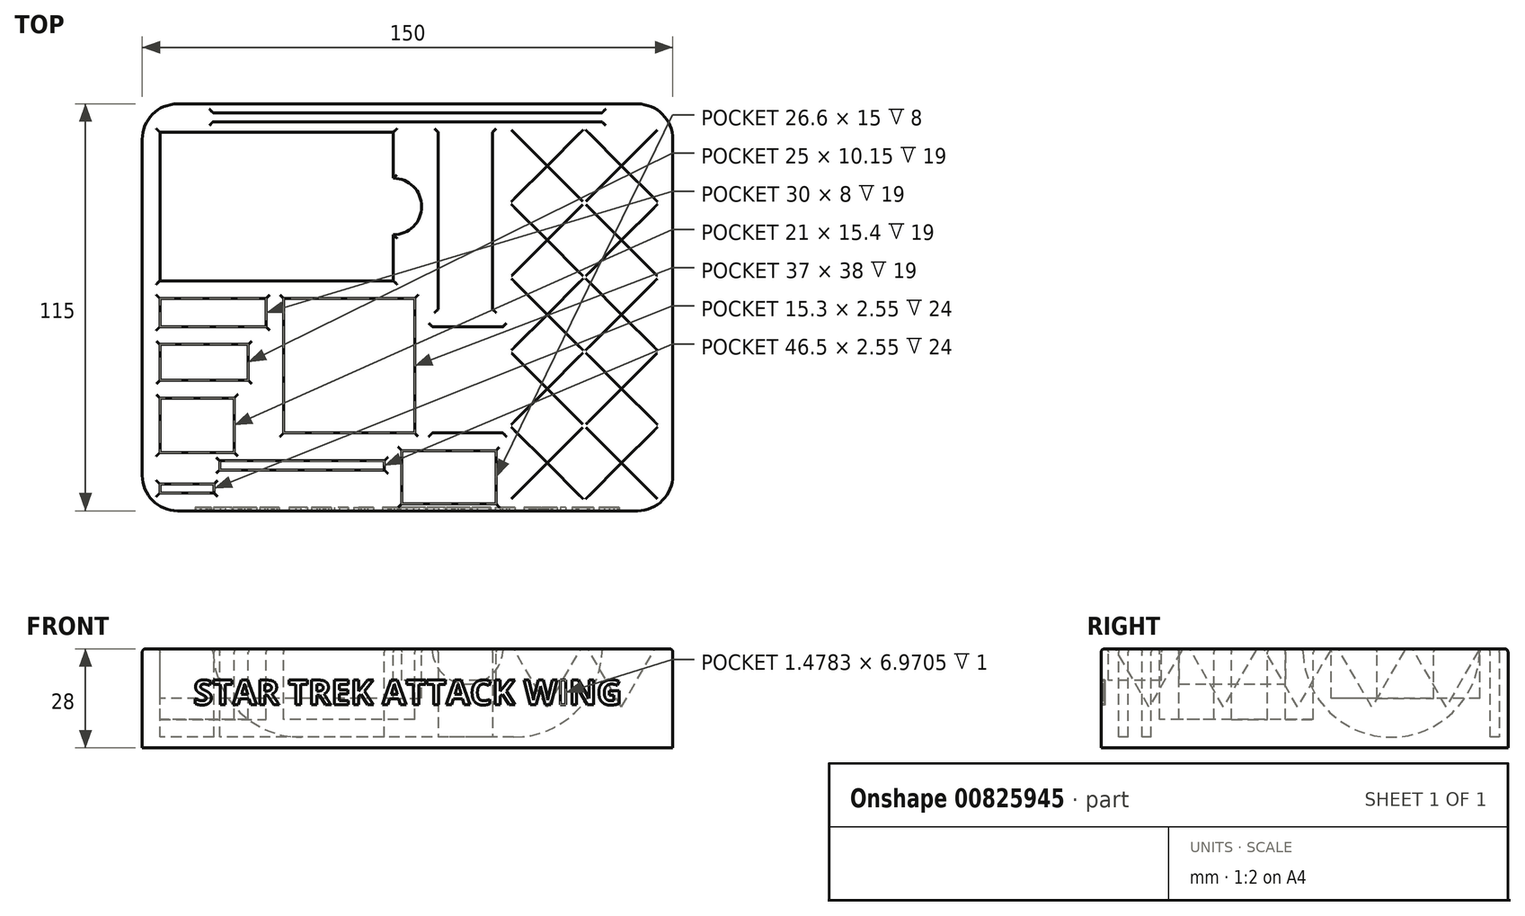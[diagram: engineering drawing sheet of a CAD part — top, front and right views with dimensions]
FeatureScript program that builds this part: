
annotation { "Feature Type Name" : "Feature", "Feature Type Description" : "" }
export const myFeature = defineFeature(function(context is Context, id is Id, definition is map)
    precondition{}
    {
        {
            var Q0;
            Q0=qCreatedBy(makeId("Top.planeOp"),FACE);
            var sketch = newSketch(context, id + "F0", { "sketchPlane" : qUnion([Q0])});
            skLineSegment(sketch, "E0.bottom", {"start": v(75, 57.5) * mm, "end": v(-75, 57.5) * mm});
            skLineSegment(sketch, "E0.top", {"start": v(75, -57.5) * mm, "end": v(-75, -57.5) * mm});
            skLineSegment(sketch, "E0.left", {"start": v(75, 57.5) * mm, "end": v(75, -57.5) * mm});
            skLineSegment(sketch, "E0.right", {"start": v(-75, 57.5) * mm, "end": v(-75, -57.5) * mm});
            skPoint(sketch, "E0.middle", {"position": v(0, 0) * mm});
            skSolve(sketch);
        }
        {
            var Q0;
            Q0 = qSketchRegion(id + "F0", true);
            extrude(context, id + "F1", {"entities" : qUnion([Q0]), "depth" : 28 * mm, "offsetDistance" : 25 * mm});
        }
        {
            var Q0;
            Q0=makeQuery(id+"F1.opExtrude","CAP_FACE",FACE,{"disambiguationData":[OSD([sQuery(id+"F0.wireOp",EDGE,"E0.bottom"),sQuery(id+"F0.wireOp",EDGE,"E0.top"),sQuery(id+"F0.wireOp",EDGE,"E0.left"),sQuery(id+"F0.wireOp",EDGE,"E0.right")])],"isStart":false});
            var sketch = newSketch(context, id + "F2", { "sketchPlane" : qUnion([Q0])});
            skLineSegment(sketch, "E1.bottom", {"start": v(-4, 49.5) * mm, "end": v(-70, 49.5) * mm});
            skLineSegment(sketch, "E1.top", {"start": v(-4, 7.5) * mm, "end": v(-70, 7.5) * mm});
            skLineSegment(sketch, "E1.left", {"start": v(-4, 49.5) * mm, "end": v(-4, 7.5) * mm});
            skLineSegment(sketch, "E1.right", {"start": v(-70, 49.5) * mm, "end": v(-70, 7.5) * mm});
            skPoint(sketch, "E1.middle", {"position": v(-37, 28.5) * mm});
            skArc(sketch, "E2", {"start": v(-4, 20.5) * mm, "mid": v(4, 28.5) * mm, "end": v(-4, 36.5) * mm});
            skSolve(sketch);
        }
        {
            var Q0;
            Q0 = qSketchRegion(id + "F2", true);
            extrude(context, id + "F3", {"entities" : qUnion([Q0]), "operationType" : NewBodyOperationType.REMOVE, "oppositeDirection" : true, "depth" : 14 * mm, "offsetDistance" : 25 * mm});
        }
        {
            var Q0;
            Q0=makeQuery(id+"F1.opExtrude","CAP_FACE",FACE,{"disambiguationData":[OSD([sQuery(id+"F0.wireOp",EDGE,"E0.bottom"),sQuery(id+"F0.wireOp",EDGE,"E0.top"),sQuery(id+"F0.wireOp",EDGE,"E0.left"),sQuery(id+"F0.wireOp",EDGE,"E0.right")])],"isStart":false});
            var sketch = newSketch(context, id + "F4", { "sketchPlane" : qUnion([Q0])});
            skLineSegment(sketch, "E3.bottom", {"start": v(70, 49.5) * mm, "end": v(51, 49.5) * mm});
            skLineSegment(sketch, "E3.top", {"start": v(70, 30.5) * mm, "end": v(51, 30.5) * mm});
            skLineSegment(sketch, "E3.left", {"start": v(70, 49.5) * mm, "end": v(70, 30.5) * mm});
            skLineSegment(sketch, "E3.right", {"start": v(51, 49.5) * mm, "end": v(51, 30.5) * mm});
            skPoint(sketch, "E3.middle", {"position": v(60.5, 40) * mm});
            skLineSegment(sketch, "E4.0.1.0", {"start": v(70, 28.5) * mm, "end": v(51, 28.5) * mm});
            skLineSegment(sketch, "E4.0.1.1", {"start": v(51, 28.5) * mm, "end": v(51, 9.5) * mm});
            skLineSegment(sketch, "E4.0.1.2", {"start": v(70, 28.5) * mm, "end": v(70, 9.5) * mm});
            skLineSegment(sketch, "E4.0.1.3", {"start": v(70, 9.5) * mm, "end": v(51, 9.5) * mm});
            skLineSegment(sketch, "E4.0.2.0", {"start": v(70, 7.5) * mm, "end": v(51, 7.5) * mm});
            skLineSegment(sketch, "E4.0.2.1", {"start": v(51, 7.5) * mm, "end": v(51, -11.5) * mm});
            skLineSegment(sketch, "E4.0.2.2", {"start": v(70, 7.5) * mm, "end": v(70, -11.5) * mm});
            skLineSegment(sketch, "E4.0.2.3", {"start": v(70, -11.5) * mm, "end": v(51, -11.5) * mm});
            skLineSegment(sketch, "E4.0.3.0", {"start": v(70, -13.5) * mm, "end": v(51, -13.5) * mm});
            skLineSegment(sketch, "E4.0.3.1", {"start": v(51, -13.5) * mm, "end": v(51, -32.5) * mm});
            skLineSegment(sketch, "E4.0.3.2", {"start": v(70, -13.5) * mm, "end": v(70, -32.5) * mm});
            skLineSegment(sketch, "E4.0.3.3", {"start": v(70, -32.5) * mm, "end": v(51, -32.5) * mm});
            skLineSegment(sketch, "E4.0.4.0", {"start": v(70, -34.5) * mm, "end": v(51, -34.5) * mm});
            skLineSegment(sketch, "E4.0.4.1", {"start": v(51, -34.5) * mm, "end": v(51, -53.5) * mm});
            skLineSegment(sketch, "E4.0.4.2", {"start": v(70, -34.5) * mm, "end": v(70, -53.5) * mm});
            skLineSegment(sketch, "E4.0.4.3", {"start": v(70, -53.5) * mm, "end": v(51, -53.5) * mm});
            skLineSegment(sketch, "E4.1.0.0", {"start": v(49, 49.5) * mm, "end": v(30, 49.5) * mm});
            skLineSegment(sketch, "E4.1.0.1", {"start": v(30, 49.5) * mm, "end": v(30, 30.5) * mm});
            skLineSegment(sketch, "E4.1.0.2", {"start": v(49, 49.5) * mm, "end": v(49, 30.5) * mm});
            skLineSegment(sketch, "E4.1.0.3", {"start": v(49, 30.5) * mm, "end": v(30, 30.5) * mm});
            skLineSegment(sketch, "E4.1.1.0", {"start": v(49, 28.5) * mm, "end": v(30, 28.5) * mm});
            skLineSegment(sketch, "E4.1.1.1", {"start": v(30, 28.5) * mm, "end": v(30, 9.5) * mm});
            skLineSegment(sketch, "E4.1.1.2", {"start": v(49, 28.5) * mm, "end": v(49, 9.5) * mm});
            skLineSegment(sketch, "E4.1.1.3", {"start": v(49, 9.5) * mm, "end": v(30, 9.5) * mm});
            skLineSegment(sketch, "E4.1.2.0", {"start": v(49, 7.5) * mm, "end": v(30, 7.5) * mm});
            skLineSegment(sketch, "E4.1.2.1", {"start": v(30, 7.5) * mm, "end": v(30, -11.5) * mm});
            skLineSegment(sketch, "E4.1.2.2", {"start": v(49, 7.5) * mm, "end": v(49, -11.5) * mm});
            skLineSegment(sketch, "E4.1.2.3", {"start": v(49, -11.5) * mm, "end": v(30, -11.5) * mm});
            skLineSegment(sketch, "E4.1.3.0", {"start": v(49, -13.5) * mm, "end": v(30, -13.5) * mm});
            skLineSegment(sketch, "E4.1.3.1", {"start": v(30, -13.5) * mm, "end": v(30, -32.5) * mm});
            skLineSegment(sketch, "E4.1.3.2", {"start": v(49, -13.5) * mm, "end": v(49, -32.5) * mm});
            skLineSegment(sketch, "E4.1.3.3", {"start": v(49, -32.5) * mm, "end": v(30, -32.5) * mm});
            skLineSegment(sketch, "E4.1.4.0", {"start": v(49, -34.5) * mm, "end": v(30, -34.5) * mm});
            skLineSegment(sketch, "E4.1.4.1", {"start": v(30, -34.5) * mm, "end": v(30, -53.5) * mm});
            skLineSegment(sketch, "E4.1.4.2", {"start": v(49, -34.5) * mm, "end": v(49, -53.5) * mm});
            skLineSegment(sketch, "E4.1.4.3", {"start": v(49, -53.5) * mm, "end": v(30, -53.5) * mm});
            skLineSegment(sketch, "E4.direction1", {"start": v(53, 70) * mm, "end": v(32, 70) * mm, "construction": true});
            skLineSegment(sketch, "E4.direction2", {"start": v(53, 70) * mm, "end": v(53, 49) * mm, "construction": true});
            skSolve(sketch);
        }
        {
            var Q0;
            Q0 = qSketchRegion(id + "F4", true);
            extrude(context, id + "F5", {"entities" : qUnion([Q0]), "operationType" : NewBodyOperationType.REMOVE, "oppositeDirection" : true, "depth" : 25 * mm, "offsetDistance" : 25 * mm, "hasDraft" : true, "draftAngle" : 30 * degree, "draftPullDirection" : true});
        }
        {
            var Q0;
            Q0=makeQuery(id+"F1.opExtrude","CAP_FACE",FACE,{"disambiguationData":[OSD([sQuery(id+"F0.wireOp",EDGE,"E0.bottom"),sQuery(id+"F0.wireOp",EDGE,"E0.top"),sQuery(id+"F0.wireOp",EDGE,"E0.left"),sQuery(id+"F0.wireOp",EDGE,"E0.right")])],"isStart":false});
            var sketch = newSketch(context, id + "F6", { "sketchPlane" : qUnion([Q0])});
            skLineSegment(sketch, "E5.bottom", {"start": v(24, 49.5) * mm, "end": v(8.7, 49.5) * mm});
            skLineSegment(sketch, "E5.top", {"start": v(24, -0.5) * mm, "end": v(8.7, -0.5) * mm});
            skLineSegment(sketch, "E5.left", {"start": v(24, 49.5) * mm, "end": v(24, -0.5) * mm});
            skLineSegment(sketch, "E5.right", {"start": v(8.7, 49.5) * mm, "end": v(8.7, -0.5) * mm});
            skPoint(sketch, "E5.middle", {"position": v(16.35, 24.5) * mm});
            skSolve(sketch);
        }
        {
            var Q0;
            Q0 = qSketchRegion(id + "F6", true);
            extrude(context, id + "F7", {"entities" : qUnion([Q0]), "operationType" : NewBodyOperationType.REMOVE, "oppositeDirection" : true, "depth" : 25 * mm, "offsetDistance" : 25 * mm});
        }
        {
            var Q0;
            Q0=makeQuery(id+"F7.boolean.opBoolean","COPY",EDGE,{"derivedFrom":makeQuery(id+"F7.opExtrude","CAP_EDGE",EDGE,{"disambiguationData":[OSD([sQuery(id+"F6.wireOp",EDGE,"E5.bottom")])],"isStart":false})});
            var Q1;
            Q1=makeQuery(id+"F7.boolean.opBoolean","COPY",EDGE,{"derivedFrom":makeQuery(id+"F7.opExtrude","CAP_EDGE",EDGE,{"disambiguationData":[OSD([sQuery(id+"F6.wireOp",EDGE,"E5.top")])],"isStart":false})});
            fillet(context, id + "F8", {"entities" : qUnion([Q0, Q1]), "radius" : 25 * mm, "tangentPropagation" : true, "allowEdgeOverflow" : false});
        }
        {
            var Q0;
            Q0=makeQuery(id+"F1.opExtrude","SWEPT_EDGE",EDGE,{"disambiguationData":[OSD([sQuery(id+"F0.wireOp",EDGE,"E0.top"),sQuery(id+"F0.wireOp",EDGE,"E0.left")])]});
            var Q1;
            Q1=makeQuery(id+"F1.opExtrude","SWEPT_EDGE",EDGE,{"disambiguationData":[OSD([sQuery(id+"F0.wireOp",EDGE,"E0.bottom"),sQuery(id+"F0.wireOp",EDGE,"E0.left")])]});
            var Q2;
            Q2=makeQuery(id+"F1.opExtrude","SWEPT_EDGE",EDGE,{"disambiguationData":[OSD([sQuery(id+"F0.wireOp",EDGE,"E0.bottom"),sQuery(id+"F0.wireOp",EDGE,"E0.right")])]});
            var Q3;
            Q3=makeQuery(id+"F1.opExtrude","SWEPT_EDGE",EDGE,{"disambiguationData":[OSD([sQuery(id+"F0.wireOp",EDGE,"E0.top"),sQuery(id+"F0.wireOp",EDGE,"E0.right")])]});
            fillet(context, id + "F9", {"entities" : qUnion([Q0, Q1, Q2, Q3]), "radius" : 10 * mm, "tangentPropagation" : true, "allowEdgeOverflow" : false});
        }
        {
            var Q0;
            Q0=makeQuery(id+"F1.opExtrude","CAP_FACE",FACE,{"disambiguationData":[OSD([sQuery(id+"F0.wireOp",EDGE,"E0.bottom"),sQuery(id+"F0.wireOp",EDGE,"E0.top"),sQuery(id+"F0.wireOp",EDGE,"E0.left"),sQuery(id+"F0.wireOp",EDGE,"E0.right")])],"isStart":false});
            var sketch = newSketch(context, id + "F10", { "sketchPlane" : qUnion([Q0])});
            skLineSegment(sketch, "E6.bottom", {"start": v(27, -5.5) * mm, "end": v(7, -5.5) * mm});
            skLineSegment(sketch, "E6.top", {"start": v(27, -35.5) * mm, "end": v(7, -35.5) * mm});
            skLineSegment(sketch, "E6.left", {"start": v(27, -5.5) * mm, "end": v(27, -35.5) * mm});
            skLineSegment(sketch, "E6.right", {"start": v(7, -5.5) * mm, "end": v(7, -35.5) * mm});
            skPoint(sketch, "E6.middle", {"position": v(17, -20.5) * mm});
            skSolve(sketch);
        }
        {
            var Q0;
            Q0 = qSketchRegion(id + "F10", true);
            extrude(context, id + "F11", {"entities" : qUnion([Q0]), "operationType" : NewBodyOperationType.REMOVE, "oppositeDirection" : true, "depth" : 10 * mm, "offsetDistance" : 25 * mm});
        }
        {
            var Q0;
            Q0=makeQuery(id+"F11.boolean.opBoolean","COPY",EDGE,{"derivedFrom":makeQuery(id+"F11.opExtrude","CAP_EDGE",EDGE,{"disambiguationData":[OSD([sQuery(id+"F10.wireOp",EDGE,"E6.left")])],"isStart":false})});
            var Q1;
            Q1=makeQuery(id+"F11.boolean.opBoolean","COPY",EDGE,{"derivedFrom":makeQuery(id+"F11.opExtrude","CAP_EDGE",EDGE,{"disambiguationData":[OSD([sQuery(id+"F10.wireOp",EDGE,"E6.right")])],"isStart":false})});
            fillet(context, id + "F12", {"entities" : qUnion([Q0, Q1]), "radius" : 10 * mm, "tangentPropagation" : true, "allowEdgeOverflow" : false});
        }
        {
            var Q0;
            Q0=makeQuery(id+"F1.opExtrude","CAP_FACE",FACE,{"disambiguationData":[OSD([sQuery(id+"F0.wireOp",EDGE,"E0.bottom"),sQuery(id+"F0.wireOp",EDGE,"E0.top"),sQuery(id+"F0.wireOp",EDGE,"E0.left"),sQuery(id+"F0.wireOp",EDGE,"E0.right")])],"isStart":false});
            var sketch = newSketch(context, id + "F13", { "sketchPlane" : qUnion([Q0])});
            skLineSegment(sketch, "E7.bottom", {"start": v(25, -40.5) * mm, "end": v(-1.6, -40.5) * mm});
            skLineSegment(sketch, "E7.top", {"start": v(25, -55.5) * mm, "end": v(-1.6, -55.5) * mm});
            skLineSegment(sketch, "E7.left", {"start": v(25, -40.5) * mm, "end": v(25, -55.5) * mm});
            skLineSegment(sketch, "E7.right", {"start": v(-1.6, -40.5) * mm, "end": v(-1.6, -55.5) * mm});
            skPoint(sketch, "E7.middle", {"position": v(11.7, -48) * mm});
            skSolve(sketch);
        }
        {
            var Q0;
            Q0 = qSketchRegion(id + "F13", true);
            extrude(context, id + "F14", {"entities" : qUnion([Q0]), "operationType" : NewBodyOperationType.REMOVE, "oppositeDirection" : true, "depth" : 9 * mm, "offsetDistance" : 25 * mm});
        }
        {
            var Q0;
            Q0=makeQuery(id+"F1.opExtrude","CAP_FACE",FACE,{"disambiguationData":[OSD([sQuery(id+"F0.wireOp",EDGE,"E0.bottom"),sQuery(id+"F0.wireOp",EDGE,"E0.top"),sQuery(id+"F0.wireOp",EDGE,"E0.left"),sQuery(id+"F0.wireOp",EDGE,"E0.right")])],"isStart":false});
            var sketch = newSketch(context, id + "F15", { "sketchPlane" : qUnion([Q0])});
            skLineSegment(sketch, "E8.bottom", {"start": v(-49, -25.65) * mm, "end": v(-70, -25.65) * mm});
            skLineSegment(sketch, "E8.top", {"start": v(-49, -41.05) * mm, "end": v(-70, -41.05) * mm});
            skLineSegment(sketch, "E8.left", {"start": v(-49, -25.65) * mm, "end": v(-49, -41.05) * mm});
            skLineSegment(sketch, "E8.right", {"start": v(-70, -25.65) * mm, "end": v(-70, -41.05) * mm});
            skPoint(sketch, "E8.middle", {"position": v(-59.5, -33.35) * mm});
            skLineSegment(sketch, "E9.bottom", {"start": v(-49, -20.65) * mm, "end": v(-70, -20.65) * mm});
            skLineSegment(sketch, "E9.top", {"start": v(-49, -10.5) * mm, "end": v(-70, -10.5) * mm});
            skLineSegment(sketch, "E9.left", {"start": v(-49, -20.65) * mm, "end": v(-49, -10.5) * mm});
            skLineSegment(sketch, "E9.right", {"start": v(-70, -20.65) * mm, "end": v(-70, -10.5) * mm});
            skPoint(sketch, "E9.middle", {"position": v(-59.5, -15.57) * mm});
            skLineSegment(sketch, "E10.bottom", {"start": v(-49, -20.65) * mm, "end": v(-45, -20.65) * mm});
            skLineSegment(sketch, "E10.top", {"start": v(-49, -10.5) * mm, "end": v(-45, -10.5) * mm});
            skLineSegment(sketch, "E10.right", {"start": v(-45, -20.65) * mm, "end": v(-45, -10.5) * mm});
            skLineSegment(sketch, "E11.bottom", {"start": v(-70, -5.5) * mm, "end": v(-40, -5.5) * mm});
            skLineSegment(sketch, "E11.top", {"start": v(-70, 2.5) * mm, "end": v(-40, 2.5) * mm});
            skLineSegment(sketch, "E11.left", {"start": v(-70, -5.5) * mm, "end": v(-70, 2.5) * mm});
            skLineSegment(sketch, "E11.right", {"start": v(-40, -5.5) * mm, "end": v(-40, 2.5) * mm});
            skSolve(sketch);
        }
        {
            var Q0;
            Q0 = qSketchRegion(id + "F15", true);
            extrude(context, id + "F16", {"entities" : qUnion([Q0]), "operationType" : NewBodyOperationType.REMOVE, "oppositeDirection" : true, "depth" : 20 * mm, "offsetDistance" : 25 * mm});
        }
        {
            var Q0;
            Q0=makeQuery(id+"F1.opExtrude","CAP_FACE",FACE,{"disambiguationData":[OSD([sQuery(id+"F0.wireOp",EDGE,"E0.bottom"),sQuery(id+"F0.wireOp",EDGE,"E0.top"),sQuery(id+"F0.wireOp",EDGE,"E0.left"),sQuery(id+"F0.wireOp",EDGE,"E0.right")])],"isStart":false});
            var sketch = newSketch(context, id + "F17", { "sketchPlane" : qUnion([Q0])});
            skLineSegment(sketch, "E12.bottom", {"start": v(2, 2.5) * mm, "end": v(-35, 2.5) * mm});
            skLineSegment(sketch, "E12.top", {"start": v(2, -35.5) * mm, "end": v(-35, -35.5) * mm});
            skLineSegment(sketch, "E12.left", {"start": v(2, 2.5) * mm, "end": v(2, -35.5) * mm});
            skLineSegment(sketch, "E12.right", {"start": v(-35, 2.5) * mm, "end": v(-35, -35.5) * mm});
            skPoint(sketch, "E12.middle", {"position": v(-16.5, -16.5) * mm});
            skSolve(sketch);
        }
        {
            var Q0;
            Q0 = qSketchRegion(id + "F17", true);
            extrude(context, id + "F18", {"entities" : qUnion([Q0]), "operationType" : NewBodyOperationType.REMOVE, "oppositeDirection" : true, "depth" : 20 * mm, "offsetDistance" : 25 * mm});
        }
        {
            var Q0;
            Q0=makeQuery(id+"F1.opExtrude","CAP_FACE",FACE,{"disambiguationData":[OSD([sQuery(id+"F0.wireOp",EDGE,"E0.bottom"),sQuery(id+"F0.wireOp",EDGE,"E0.top"),sQuery(id+"F0.wireOp",EDGE,"E0.left"),sQuery(id+"F0.wireOp",EDGE,"E0.right")])],"isStart":false});
            var sketch = newSketch(context, id + "F19", { "sketchPlane" : qUnion([Q0])});
            skLineSegment(sketch, "E13.bottom", {"start": v(-54.7, -49.95) * mm, "end": v(-70, -49.95) * mm});
            skLineSegment(sketch, "E13.top", {"start": v(-54.7, -52.5) * mm, "end": v(-70, -52.5) * mm});
            skLineSegment(sketch, "E13.left", {"start": v(-54.7, -49.95) * mm, "end": v(-54.7, -52.5) * mm});
            skLineSegment(sketch, "E13.right", {"start": v(-70, -49.95) * mm, "end": v(-70, -52.5) * mm});
            skPoint(sketch, "E13.middle", {"position": v(-62.35, -51.22) * mm});
            skSolve(sketch);
        }
        {
            var Q0;
            Q0 = qSketchRegion(id + "F19", true);
            extrude(context, id + "F20", {"entities" : qUnion([Q0]), "operationType" : NewBodyOperationType.REMOVE, "oppositeDirection" : true, "depth" : 25 * mm, "offsetDistance" : 25 * mm});
        }
        {
            var Q0;
            Q0=makeQuery(id+"F1.opExtrude","CAP_FACE",FACE,{"disambiguationData":[OSD([sQuery(id+"F0.wireOp",EDGE,"E0.bottom"),sQuery(id+"F0.wireOp",EDGE,"E0.top"),sQuery(id+"F0.wireOp",EDGE,"E0.left"),sQuery(id+"F0.wireOp",EDGE,"E0.right")])],"isStart":false});
            var sketch = newSketch(context, id + "F21", { "sketchPlane" : qUnion([Q0])});
            skLineSegment(sketch, "E14.bottom", {"start": v(-6.6, -43.4) * mm, "end": v(-53.1, -43.4) * mm});
            skLineSegment(sketch, "E14.top", {"start": v(-6.6, -45.95) * mm, "end": v(-53.1, -45.95) * mm});
            skLineSegment(sketch, "E14.left", {"start": v(-6.6, -43.4) * mm, "end": v(-6.6, -45.95) * mm});
            skLineSegment(sketch, "E14.right", {"start": v(-53.1, -43.4) * mm, "end": v(-53.1, -45.95) * mm});
            skPoint(sketch, "E14.middle", {"position": v(-29.85, -44.68) * mm});
            skSolve(sketch);
        }
        {
            var Q0;
            Q0=makeQuery(id+"F21.imprint","IMPRINT",FACE,{"disambiguationData":[TD([[makeQuery(id+"F21.imprint","IMPRINT",EDGE,{"derivedFrom":sQuery(id+"F21.wireOp",EDGE,"E14.bottom")}),1.0]])]});
            extrude(context, id + "F22", {"entities" : qUnion([Q0]), "operationType" : NewBodyOperationType.REMOVE, "oppositeDirection" : true, "depth" : 25 * mm, "offsetDistance" : 25 * mm});
        }
        {
            var Q0;
            Q0=makeQuery(id+"F1.opExtrude","SWEPT_FACE",FACE,{"disambiguationData":[OSD([sQuery(id+"F0.wireOp",EDGE,"E0.top")])]});
            var sketch = newSketch(context, id + "F23", { "sketchPlane" : qUnion([Q0])});
            skText(sketch, "E15", { "text": "STAR TREK ATTACK WING", "fontName": "OpenSans-Bold.ttf"});
            const initialGuessF23  = {"E15": [-0.06045, 0.01217, 1, 0, 0.00703]};
            skSetInitialGuess(sketch, initialGuessF23);
            skSolve(sketch);
        }
        {
            var Q0;
            Q0 = qSketchRegion(id + "F23", true);
            extrude(context, id + "F24", {"entities" : qUnion([Q0]), "operationType" : NewBodyOperationType.REMOVE, "oppositeDirection" : true, "depth" : 1 * mm, "offsetDistance" : 25 * mm});
        }
        {
            var Q0;
            Q0=makeQuery(id+"F1.opExtrude","CAP_FACE",FACE,{"disambiguationData":[OSD([sQuery(id+"F0.wireOp",EDGE,"E0.bottom"),sQuery(id+"F0.wireOp",EDGE,"E0.top"),sQuery(id+"F0.wireOp",EDGE,"E0.left"),sQuery(id+"F0.wireOp",EDGE,"E0.right")])],"isStart":false});
            var sketch = newSketch(context, id + "F25", { "sketchPlane" : qUnion([Q0])});
            skLineSegment(sketch, "E16.bottom", {"start": v(55, 55) * mm, "end": v(-55, 55) * mm});
            skLineSegment(sketch, "E16.top", {"start": v(55, 52.45) * mm, "end": v(-55, 52.45) * mm});
            skLineSegment(sketch, "E16.left", {"start": v(55, 55) * mm, "end": v(55, 52.45) * mm});
            skLineSegment(sketch, "E16.right", {"start": v(-55, 55) * mm, "end": v(-55, 52.45) * mm});
            skPoint(sketch, "E16.middle", {"position": v(0, 53.73) * mm});
            skSolve(sketch);
        }
        {
            var Q0;
            Q0 = qSketchRegion(id + "F25", true);
            extrude(context, id + "F26", {"entities" : qUnion([Q0]), "operationType" : NewBodyOperationType.REMOVE, "oppositeDirection" : true, "depth" : 25 * mm, "offsetDistance" : 25 * mm});
        }
        {
            var Q0;
            Q0=makeQuery(id+"F26.boolean.opBoolean","COPY",EDGE,{"derivedFrom":makeQuery(id+"F26.opExtrude","CAP_EDGE",EDGE,{"disambiguationData":[OSD([sQuery(id+"F25.wireOp",EDGE,"E16.right")])],"isStart":false})});
            var Q1;
            Q1=makeQuery(id+"F26.boolean.opBoolean","COPY",EDGE,{"derivedFrom":makeQuery(id+"F26.opExtrude","CAP_EDGE",EDGE,{"disambiguationData":[OSD([sQuery(id+"F25.wireOp",EDGE,"E16.left")])],"isStart":false})});
            fillet(context, id + "F27", {"entities" : qUnion([Q0, Q1]), "radius" : 25 * mm, "tangentPropagation" : true, "allowEdgeOverflow" : false});
        }
        {
            var Q0;
            Q0=makeQuery(id+"F1.opExtrude","CAP_FACE",FACE,{"disambiguationData":[OSD([sQuery(id+"F0.wireOp",EDGE,"E0.bottom"),sQuery(id+"F0.wireOp",EDGE,"E0.top"),sQuery(id+"F0.wireOp",EDGE,"E0.left"),sQuery(id+"F0.wireOp",EDGE,"E0.right")])],"isStart":false});
            fillet(context, id + "F28", {"entities" : qUnion([Q0]), "radius" : 1 * mm, "tangentPropagation" : true, "allowEdgeOverflow" : false});
        }
    });
